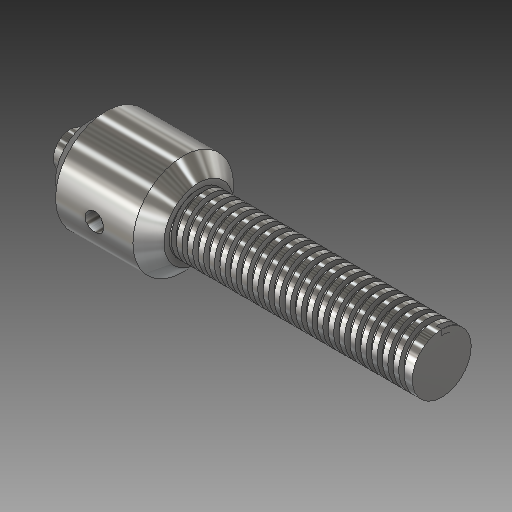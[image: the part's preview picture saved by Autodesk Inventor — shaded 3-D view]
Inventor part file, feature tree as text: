
AUTODESK INVENTOR PART (.ipt)
format: ipt  version: 2018 (Build 220112000, 112)  size: 577,024 bytes
history: native  units: in
note: dims shown in document units (in); Inventor stores cm internally (conversion verified against a paired STEP export)
features: sketch x4, extrude x2, revolve x1, helix x1, thread x1
ambient origin geometry x8: Origin, YZ Plane, XZ Plane, XY Plane, X Axis, Y Axis, Z Axis, Center Point
bodies: Solid1 (feature_tree)
feature tree (9):
  revolve  "Revolution1"  [1 undecoded]
  helix  "Coil1"  [1 undecoded]
  extrude  "Extrusion1"  Depth=0.3937in
  extrude  "Extrusion2"  Depth=1.378in
  thread  "Thread1"  [1 undecoded]
  sketch  "Sketch1"  dims[d0=0.4331in d3=0.748in d5=0.4528in]
  sketch  "Sketch2"  dims[d10=90.0deg]
  sketch  "Sketch3"  dims[d14=0.2756in d15=6.1417in d16=0.3937in d17=0.0in d18=90.0deg d19=90.0deg d20=0.0in d21=0.0in d22=0.4724in]
  sketch  "Sketch4"  dims[d23=0.3937in d24=0.0in d25=0.4724in d26=1.378in d27=0.0in d28=1.1811in d29=0.1969in]
note: 3 required parameter values undecoded (feature->parameter linkage not recoverable at this tier; creation-order binding heuristic only, values carry confidence <= 0.55)